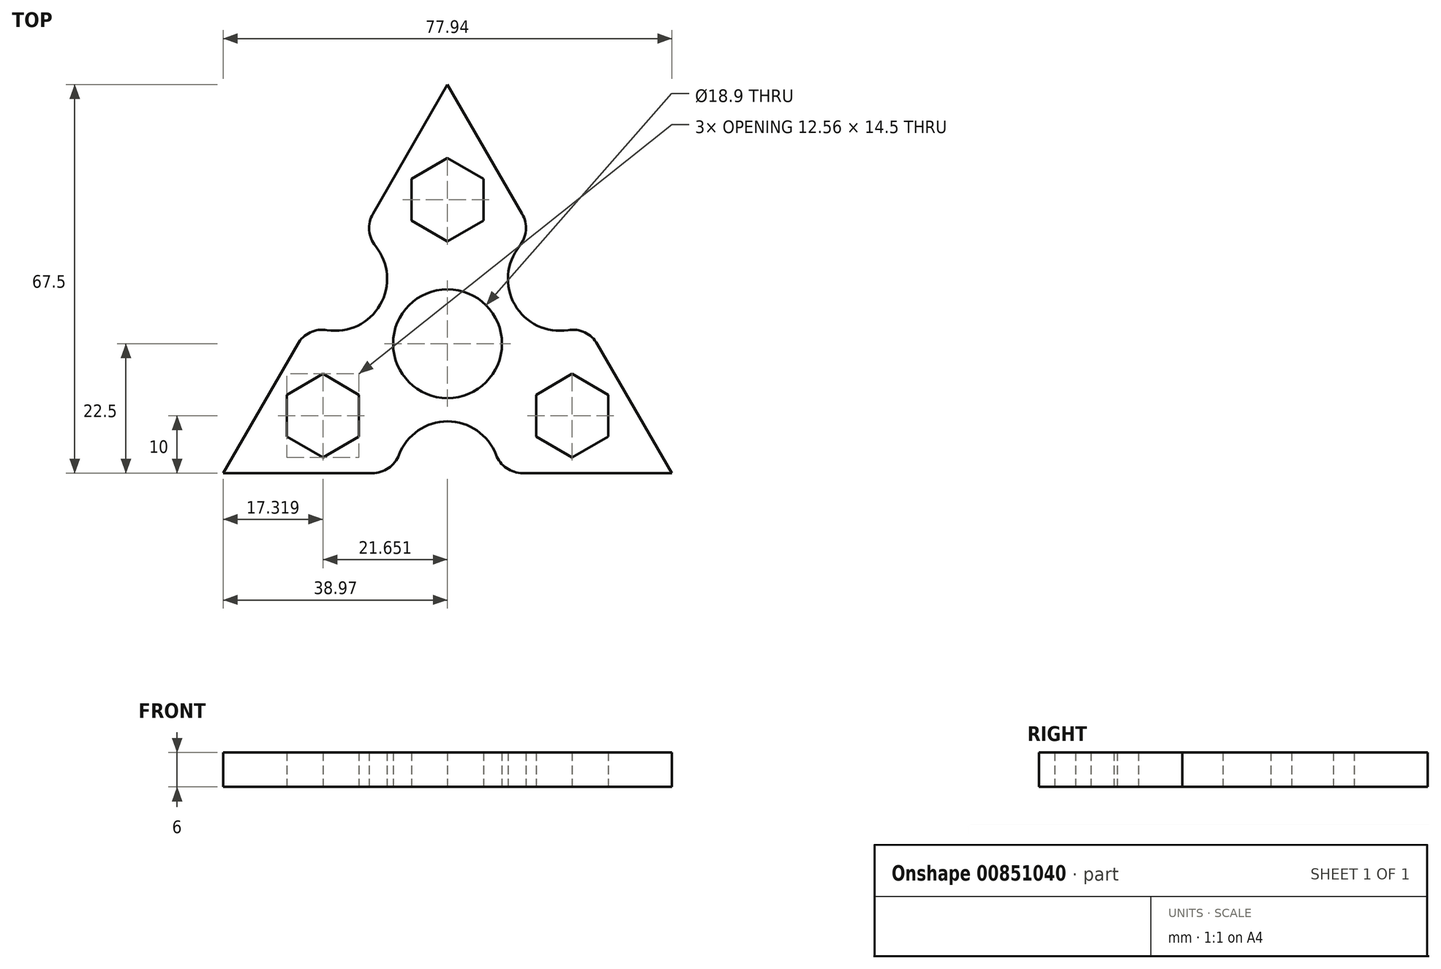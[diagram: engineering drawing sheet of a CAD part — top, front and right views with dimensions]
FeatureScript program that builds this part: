
annotation { "Feature Type Name" : "Feature", "Feature Type Description" : "" }
export const myFeature = defineFeature(function(context is Context, id is Id, definition is map)
    precondition{}
    {
        {
            var Q0;
            Q0=qCreatedBy(makeId("Top.planeOp"),FACE);
            var sketch = newSketch(context, id + "F0", { "sketchPlane" : qUnion([Q0])});
            skCircle(sketch, "E0", {"center": v(0, 0) * mm, "radius": 45 * mm, "construction": true});
            skLineSegment(sketch, "E1.0", {"start": v(0, 45) * mm, "end": v(38.97, -22.5) * mm});
            skLineSegment(sketch, "E1.1", {"start": v(38.97, -22.5) * mm, "end": v(-38.97, -22.5) * mm});
            skLineSegment(sketch, "E1.2", {"start": v(-38.97, -22.5) * mm, "end": v(0, 45) * mm});
            skLineSegment(sketch, "E2", {"start": v(0, 45) * mm, "end": v(0, -22.5) * mm, "construction": true});
            skLineSegment(sketch, "E3.1.0", {"start": v(-38.97, -22.5) * mm, "end": v(19.49, 11.25) * mm, "construction": true});
            skLineSegment(sketch, "E3.2.0", {"start": v(38.97, -22.5) * mm, "end": v(-19.49, 11.25) * mm, "construction": true});
            skArc(sketch, "E4", {"start": v(14.99, 19.04) * mm, "mid": v(11.7, 6.75) * mm, "end": v(23.99, 3.46) * mm});
            skCircle(sketch, "E5", {"center": v(0, 0) * mm, "radius": 9.45 * mm});
            skPoint(sketch, "E6.center", {"position": v(-8.35, -4.82) * mm});
            skArc(sketch, "E7.1.0", {"start": v(-23.99, 3.46) * mm, "mid": v(-11.7, 6.75) * mm, "end": v(-14.99, 19.04) * mm});
            skArc(sketch, "E7.2.0", {"start": v(9, -22.5) * mm, "mid": v(0, -13.5) * mm, "end": v(-9, -22.5) * mm});
            skPoint(sketch, "E8", {"position": v(0, 25) * mm});
            skCircle(sketch, "E9.cCircle", {"center": v(0, 25) * mm, "radius": 7.25 * mm, "construction": true});
            skLineSegment(sketch, "E9.0", {"start": v(0, 32.25) * mm, "end": v(6.28, 28.63) * mm});
            skLineSegment(sketch, "E9.1", {"start": v(6.28, 28.62) * mm, "end": v(6.28, 21.37) * mm});
            skLineSegment(sketch, "E9.2", {"start": v(6.28, 21.37) * mm, "end": v(0, 17.75) * mm});
            skLineSegment(sketch, "E9.3", {"start": v(0, 17.75) * mm, "end": v(-6.28, 21.37) * mm});
            skLineSegment(sketch, "E9.4", {"start": v(-6.28, 21.37) * mm, "end": v(-6.28, 28.62) * mm});
            skLineSegment(sketch, "E9.5", {"start": v(-6.28, 28.62) * mm, "end": v(0, 32.25) * mm});
            skPoint(sketch, "E10.center", {"position": v(4.33, 7.5) * mm});
            skLineSegment(sketch, "E11.1.0", {"start": v(-21.65, -19.75) * mm, "end": v(-27.93, -16.12) * mm});
            skLineSegment(sketch, "E11.1.1", {"start": v(-27.93, -16.12) * mm, "end": v(-27.93, -8.87) * mm});
            skLineSegment(sketch, "E11.1.2", {"start": v(-27.93, -8.87) * mm, "end": v(-21.65, -5.25) * mm});
            skLineSegment(sketch, "E11.1.3", {"start": v(-21.65, -5.25) * mm, "end": v(-15.37, -8.87) * mm});
            skLineSegment(sketch, "E11.1.4", {"start": v(-15.37, -8.87) * mm, "end": v(-15.37, -16.12) * mm});
            skLineSegment(sketch, "E11.1.5", {"start": v(-15.37, -16.12) * mm, "end": v(-21.65, -19.75) * mm});
            skLineSegment(sketch, "E11.2.0", {"start": v(27.93, -8.87) * mm, "end": v(27.93, -16.12) * mm});
            skLineSegment(sketch, "E11.2.1", {"start": v(27.93, -16.13) * mm, "end": v(21.65, -19.75) * mm});
            skLineSegment(sketch, "E11.2.2", {"start": v(21.65, -19.75) * mm, "end": v(15.37, -16.13) * mm});
            skLineSegment(sketch, "E11.2.3", {"start": v(15.37, -16.13) * mm, "end": v(15.37, -8.87) * mm});
            skLineSegment(sketch, "E11.2.4", {"start": v(15.37, -8.87) * mm, "end": v(21.65, -5.25) * mm});
            skLineSegment(sketch, "E11.2.5", {"start": v(21.65, -5.25) * mm, "end": v(27.93, -8.87) * mm});
            skSolve(sketch);
        }
        {
            var Q0;
            {var subQ4=sQuery(id+"F0.wireOp",EDGE,"E4");Q0=makeQuery(id+"F0.imprint","IMPRINT",FACE,{"disambiguationData":[TD([[makeQuery(id+"F0.imprint","IMPRINT",EDGE,{"derivedFrom":subQ4}),-1.0]])]});}
            extrude(context, id + "F1", {"entities" : qUnion([Q0]), "depth" : 6 * mm, "offsetDistance" : 25 * mm});
        }
        {
            var Q0;
            {var subQ0=sQuery(id+"F0.wireOp",EDGE,"E4");var subQ1=sQuery(id+"F0.wireOp",EDGE,"E1.0");Q0=makeQuery(id+"F1.opExtrude","SWEPT_EDGE",EDGE,{"disambiguationData":[OSD([subQ1,subQ0]),TDD([makeQuery(id+"F0.imprint","INTERSECT",VERTEX,{"disambiguationData":[OD(0.0)],"derivedFrom":[subQ1,subQ0]})])]});}
            var Q1;
            {var subQ0=sQuery(id+"F0.wireOp",EDGE,"E7.1.0");var subQ1=sQuery(id+"F0.wireOp",EDGE,"E1.2");Q1=makeQuery(id+"F1.opExtrude","SWEPT_EDGE",EDGE,{"disambiguationData":[OSD([subQ1,subQ0]),TDD([makeQuery(id+"F0.imprint","INTERSECT",VERTEX,{"disambiguationData":[OD(1.0)],"derivedFrom":[subQ1,subQ0]})])]});}
            var Q2;
            {var subQ0=sQuery(id+"F0.wireOp",EDGE,"E7.1.0");var subQ1=sQuery(id+"F0.wireOp",EDGE,"E1.2");Q2=makeQuery(id+"F1.opExtrude","SWEPT_EDGE",EDGE,{"disambiguationData":[OSD([subQ1,subQ0]),TDD([makeQuery(id+"F0.imprint","INTERSECT",VERTEX,{"disambiguationData":[OD(0.0)],"derivedFrom":[subQ1,subQ0]})])]});}
            var Q3;
            {var subQ0=sQuery(id+"F0.wireOp",EDGE,"E7.2.0");var subQ1=sQuery(id+"F0.wireOp",EDGE,"E1.1");Q3=makeQuery(id+"F1.opExtrude","SWEPT_EDGE",EDGE,{"disambiguationData":[OSD([subQ1,subQ0]),TDD([makeQuery(id+"F0.imprint","INTERSECT",VERTEX,{"disambiguationData":[OD(1.0)],"derivedFrom":[subQ1,subQ0]})])]});}
            var Q4;
            {var subQ0=sQuery(id+"F0.wireOp",EDGE,"E7.2.0");var subQ1=sQuery(id+"F0.wireOp",EDGE,"E1.1");Q4=makeQuery(id+"F1.opExtrude","SWEPT_EDGE",EDGE,{"disambiguationData":[OSD([subQ1,subQ0]),TDD([makeQuery(id+"F0.imprint","INTERSECT",VERTEX,{"disambiguationData":[OD(0.0)],"derivedFrom":[subQ1,subQ0]})])]});}
            var Q5;
            {var subQ0=sQuery(id+"F0.wireOp",EDGE,"E4");var subQ1=sQuery(id+"F0.wireOp",EDGE,"E1.0");Q5=makeQuery(id+"F1.opExtrude","SWEPT_EDGE",EDGE,{"disambiguationData":[OSD([subQ1,subQ0]),TDD([makeQuery(id+"F0.imprint","INTERSECT",VERTEX,{"disambiguationData":[OD(1.0)],"derivedFrom":[subQ1,subQ0]})])]});}
            fillet(context, id + "F2", {"entities" : qUnion([Q0, Q1, Q2, Q3, Q4, Q5]), "radius" : 5 * mm, "tangentPropagation" : true, "allowEdgeOverflow" : false});
        }
    });
